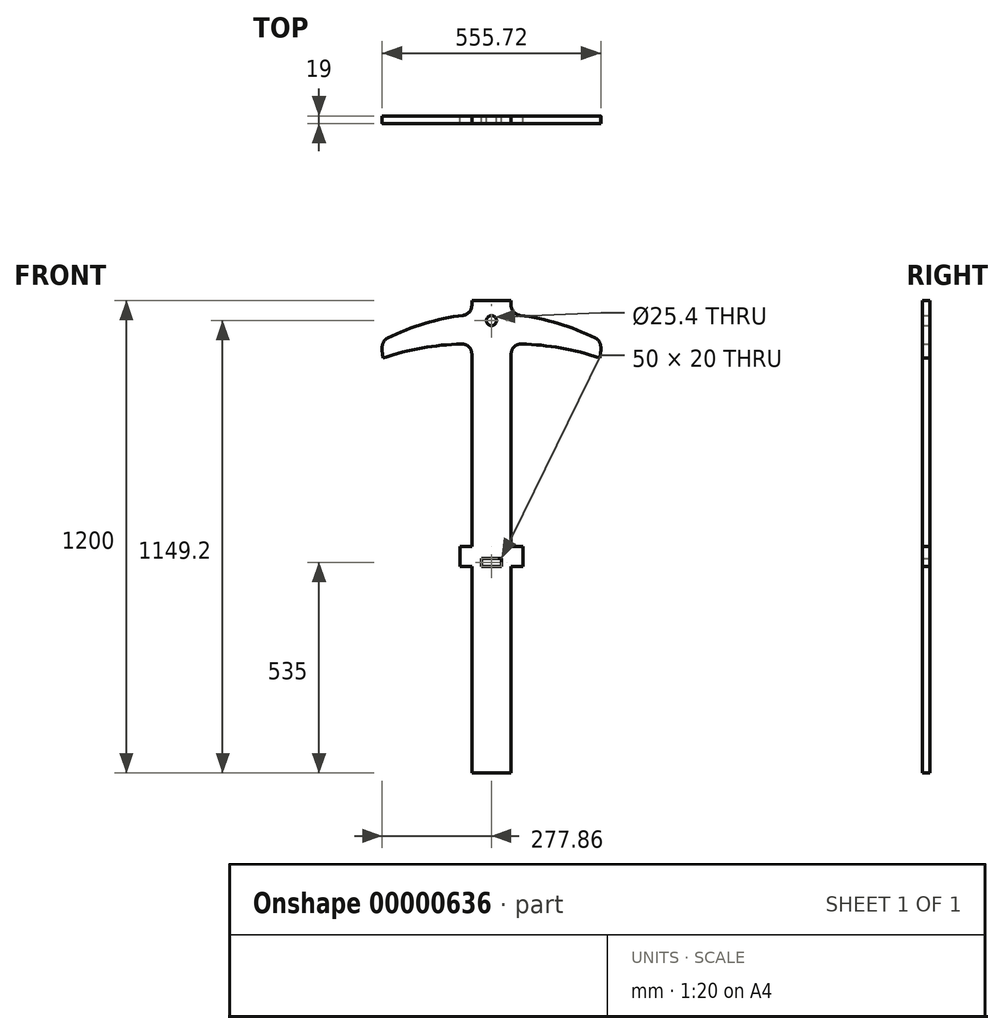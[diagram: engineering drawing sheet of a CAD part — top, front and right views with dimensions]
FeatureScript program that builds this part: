
annotation { "Feature Type Name" : "Feature", "Feature Type Description" : "" }
export const myFeature = defineFeature(function(context is Context, id is Id, definition is map)
    precondition{}
    {
        {
            var Q0;
            Q0=qCreatedBy(makeId("Front.planeOp"),FACE);
            var sketch = newSketch(context, id + "F0", { "sketchPlane" : qUnion([Q0])});
            skLineSegment(sketch, "E0.rect.bottom", {"start": v(-50, 600) * mm, "end": v(50, 600) * mm});
            skLineSegment(sketch, "E0.rect.top", {"start": v(-50, -600) * mm, "end": v(50, -600) * mm});
            skLineSegment(sketch, "E0.rect.left", {"start": v(-50, 600) * mm, "end": v(-50, 587.4) * mm});
            skLineSegment(sketch, "E0.rect.right", {"start": v(50, 600) * mm, "end": v(50, 587.4) * mm});
            skPoint(sketch, "E0.rect.middle", {"position": v(0, 0) * mm});
            skLineSegment(sketch, "E1.bottom", {"start": v(-50, -75) * mm, "end": v(-80, -75) * mm});
            skLineSegment(sketch, "E1.top", {"start": v(-50, -25) * mm, "end": v(-80, -25) * mm});
            skLineSegment(sketch, "E1.right", {"start": v(-80, -75) * mm, "end": v(-80, -25) * mm});
            skLineSegment(sketch, "E2.bottom", {"start": v(50, -75) * mm, "end": v(80, -75) * mm});
            skLineSegment(sketch, "E2.top", {"start": v(50, -25) * mm, "end": v(80, -25) * mm});
            skLineSegment(sketch, "E2.right", {"start": v(80, -75) * mm, "end": v(80, -25) * mm});
            skLineSegment(sketch, "E3.trimOffspring", {"start": v(50, -75) * mm, "end": v(50, -600) * mm});
            skLineSegment(sketch, "E4.trimOffspring", {"start": v(-50, -75) * mm, "end": v(-50, -600) * mm});
            skLineSegment(sketch, "E5.bottom", {"start": v(-25, -55) * mm, "end": v(25, -55) * mm});
            skLineSegment(sketch, "E5.top", {"start": v(-25, -75) * mm, "end": v(25, -75) * mm});
            skLineSegment(sketch, "E5.left", {"start": v(-25, -55) * mm, "end": v(-25, -75) * mm});
            skLineSegment(sketch, "E5.right", {"start": v(25, -55) * mm, "end": v(25, -75) * mm});
            skLineSegment(sketch, "E6", {"start": v(0, -55) * mm, "end": v(0, 0) * mm, "construction": true});
            skArc(sketch, "E7", {"start": v(-71.82, 562.6) * mm, "mid": v(-170.09, 541.7) * mm, "end": v(-263.61, 505) * mm});
            skArc(sketch, "E8", {"start": v(-75.68, 489.79) * mm, "mid": v(-176.67, 479.47) * mm, "end": v(-275, 454.26) * mm});
            skArc(sketch, "E9", {"start": v(263.61, 505) * mm, "mid": v(170.09, 541.7) * mm, "end": v(71.82, 562.6) * mm});
            skArc(sketch, "E10", {"start": v(275, 454.26) * mm, "mid": v(176.67, 479.47) * mm, "end": v(75.68, 489.79) * mm});
            skArc(sketch, "E11", {"start": v(-277.5, 484.78) * mm, "mid": v(-277.56, 469.42) * mm, "end": v(-275, 454.26) * mm});
            skArc(sketch, "E12", {"start": v(275, 454.26) * mm, "mid": v(277.56, 469.42) * mm, "end": v(277.5, 484.78) * mm});
            skPoint(sketch, "E13.visualSharp", {"position": v(-275, 499.26) * mm});
            skPoint(sketch, "E14.visualSharp", {"position": v(275, 499.26) * mm});
            skArc(sketch, "E14.filletArc", {"start": v(277.5, 484.78) * mm, "mid": v(273.2, 496.71) * mm, "end": v(263.61, 505) * mm});
            skLineSegment(sketch, "E15.trimOffspring", {"start": v(-50, 464.8) * mm, "end": v(-50, -25) * mm});
            skLineSegment(sketch, "E16.trimOffspring", {"start": v(50, 464.8) * mm, "end": v(50, -25) * mm});
            skPoint(sketch, "E17.visualSharp", {"position": v(-50, 565) * mm});
            skArc(sketch, "E17.filletArc", {"start": v(-71.82, 562.6) * mm, "mid": v(-56.23, 570.88) * mm, "end": v(-50, 587.4) * mm});
            skPoint(sketch, "E18.visualSharp", {"position": v(50, 565) * mm});
            skArc(sketch, "E18.filletArc", {"start": v(50, 587.4) * mm, "mid": v(56.23, 570.88) * mm, "end": v(71.82, 562.6) * mm});
            skPoint(sketch, "E19.visualSharp", {"position": v(50, 490) * mm});
            skArc(sketch, "E19.filletArc", {"start": v(75.68, 489.79) * mm, "mid": v(57.56, 482.71) * mm, "end": v(50, 464.8) * mm});
            skPoint(sketch, "E20.visualSharp", {"position": v(-50, 490) * mm});
            skArc(sketch, "E20.filletArc", {"start": v(-50, 464.8) * mm, "mid": v(-57.56, 482.71) * mm, "end": v(-75.68, 489.79) * mm});
            skArc(sketch, "E21.filletArc", {"start": v(-263.61, 505) * mm, "mid": v(-273.2, 496.71) * mm, "end": v(-277.5, 484.78) * mm});
            skCircle(sketch, "E22", {"center": v(0, 549.2) * mm, "radius": 12.7 * mm});
            skLineSegment(sketch, "E23", {"start": v(0, 549.2) * mm, "end": v(0, 600) * mm});
            skSolve(sketch);
        }
        {
            var Q0;
            Q0=makeQuery(id+"F0.imprint","IMPRINT",FACE,{"disambiguationData":[TD([[makeQuery(id+"F0.imprint","IMPRINT",EDGE,{"derivedFrom":sQuery(id+"F0.wireOp",EDGE,"E0.rect.top")}),1.0]])]});
            extrude(context, id + "F1", {"entities" : qUnion([Q0]), "depth" : 19 * mm});
        }
    });
